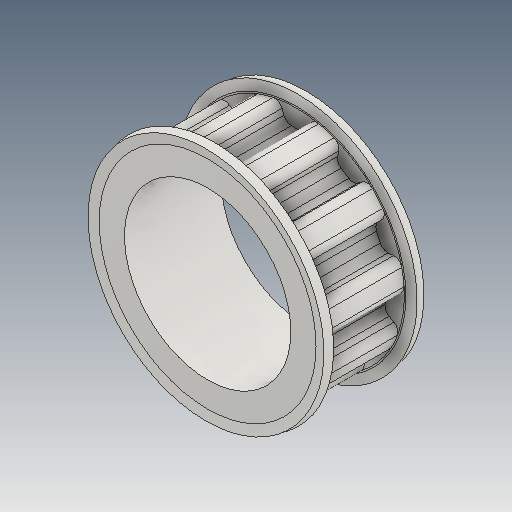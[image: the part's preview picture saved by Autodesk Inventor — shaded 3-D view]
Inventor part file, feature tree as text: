
AUTODESK INVENTOR PART (.ipt)
format: ipt  version: 2020.3 (Build 243373010, 373A)  size: 352,256 bytes
history: native  units: mm (DEFAULTED — no unit token found)
features: other x3, extrude x3, sketch x2, fillet x1, pattern_circular x1
ambient origin geometry x8: Origin, YZ Plane, XZ Plane, XY Plane, X Axis, Y Axis, Z Axis, Center Point
bodies: Solid1 (feature_tree)
feature tree (10):
  other  "Pulley Sketch"
  extrude  "Base Body"  Depth=0.381mm
  extrude  "Tooth"  Depth=1.1684mm
  fillet  "Tooth Fillet"  Radius=3.048mm
  pattern_circular  "Teeth"  [2 undecoded]
  other  "Left flange"
  other  "Right flange"
  sketch  "Sketch2"  dims[d0=33.350918mm d1=0.381mm]
  extrude  "Extrusion3"  TaperAngle=0.0deg  [1 undecoded]
  sketch  "Sketch3"  dims[d2=2.667mm d3=6.981317mm d4=3.048mm d5=12.0mm d6=0.0mm d7=12.0mm d8=0.0mm d9=1.1938mm d10=1.1684mm d11=110.0mm d12=360.0deg d15=0.0mm d16=0.0mm d17=25.0mm d18=0.252mm d19=0.0mm]
note: 3 required parameter values undecoded (feature->parameter linkage not recoverable at this tier; creation-order binding heuristic only, values carry confidence <= 0.55)
